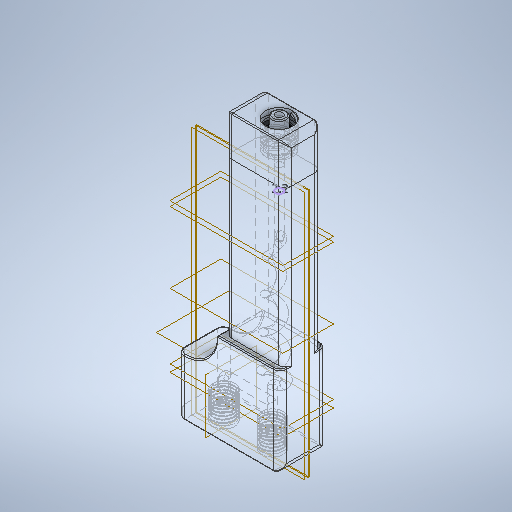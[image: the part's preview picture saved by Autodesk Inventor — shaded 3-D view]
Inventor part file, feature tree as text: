
AUTODESK INVENTOR PART (.ipt)
format: ipt  version: 2025 (Build 290162000, 162)  size: 1,564,672 bytes
history: native  units: mm
features: sketch x27, extrude x15, plane x11, other x9, revolve x6, fillet x3, projected_geometry x1
ambient origin geometry x8: Origin, YZ Plane, XZ Plane, XY Plane, X Axis, Y Axis, Z Axis, Center Point
bodies: Volumenkörper1 (feature_tree), Volumenkörper4 (feature_tree), Volumenkörper5 (feature_tree), Volumenkörper6 (feature_tree), Volumenkörper7 (feature_tree)
feature tree (72):
  extrude  "Extrusion1"  Depth=14.0mm
  extrude  "Extrusion2"  Depth=6.584mm
  plane  "Arbeitsebene4"
  extrude  "Extrusion3"  Depth=2.2mm
  extrude  "Extrusion8"  TaperAngle=0.0deg  [1 undecoded]
  revolve  "Umdrehung3"
  plane  "Arbeitsebene12"
  extrude  "Extrusion10"  Depth=5.0mm TaperAngle=0.0deg
  plane  "Arbeitsebene7"
  extrude  "Extrusion13"  Depth=2.2mm TaperAngle=0.0deg
  extrude  "Extrusion14"  Depth=2.8mm TaperAngle=0.0deg
  other  "Spirale2"
  revolve  "Umdrehung9"
  extrude  "Extrusion15"  Depth=11.0mm
  revolve  "Umdrehung10"
  extrude  "Extrusion16"  Depth=50.0mm TaperAngle=0.0deg
  sketch  "Skizze32"  dims[d91=5.818mm d92=8.0mm d93=-0.061087mm]
  plane  "Arbeitsebene14"
  revolve  "Umdrehung11"
  plane  "Arbeitsebene15"
  plane  "Arbeitsebene16"
  revolve  "Umdrehung12"
  plane  "Arbeitsebene17"
  extrude  "Extrusion19"  TaperAngle=90.0deg  [1 undecoded]
  extrude  "Extrusion20"  Depth=8.15mm
  revolve  "Umdrehung14"
  plane  "Arbeitsebene18"
  other  "Spirale3"
  fillet  "Rundung1"  Radius=13.6mm
  fillet  "Rundung2"  [1 undecoded]
  sketch  "Skizze44"  dims[d111=9.0mm d112=-0.300197mm]
  plane  "Arbeitsebene19"
  other  "Trennen1"
  other  "Körper verschieben1"
  extrude  "Extrusion21"  Depth=7.52mm
  other  "Kombinieren1"
  plane  "Arbeitsebene20"
  extrude  "Extrusion22"  Depth=8.0mm
  extrude  "Extrusion23"  Depth=1.1mm
  fillet  "Rundung4"  Radius=2.2mm
  plane  "Arbeitsebene21"
  other  "Spirale4"
  other  "Spirale5"
  sketch  "Skizze49"  dims[d125=5.0mm d126=10.0mm d127=12.5mm d128=0.061087mm d129=90.0deg d130=90.0deg d131=0.0mm d132=0.0mm]
  other  "Trennen3"
  other  "Körper verschieben2"
  extrude  "Extrusion24"  Depth=54.45mm
  sketch  "Skizze1"  dims[d0=31.0mm d1=14.0mm]
  sketch  "Skizze2"  dims[d2=11.0mm d3=0.0mm d4=6.584mm]
  sketch  "Skizze3"  dims[d6=8.0mm d7=0.0mm d8=2.2mm]
  sketch  "Skizze10"  dims[d9=2.2mm d11=0.0mm]
  sketch  "Skizze11"  dims[d12=8.0mm d13=0.0mm d24=5.0mm d25=0.0mm]
  sketch  "Skizze15"  dims[d26=90.0deg d33=2.2mm d34=0.0mm]
  sketch  "Skizze23"  dims[d35=13.2mm d60=2.8mm d61=0.0mm]
  sketch  "Skizze24"  dims[d62=18.0mm d63=11.0mm]
  sketch  "Skizze25"  dims[d64=1.5mm d65=50.0mm d66=0.0mm]
  sketch  "Skizze27"  dims[d70=8.75mm]
  sketch  "Skizze29"  dims[d71=10.0mm d72=10.0mm d73=35.0mm d74=-0.436332mm d75=90.0deg d76=90.0deg d77=0.0mm d78=0.0mm d80=90.0deg]
  sketch  "Skizze30"  dims[d81=5.9mm d84=8.15mm d86=13.6mm d87=0.0mm d88=90.0deg]
  sketch  "Skizze31"  dims[d89=8.13mm d90=7.52mm]
  sketch  "Skizze35"  dims[d100=0.0mm d102=1.1mm d103=2.2mm]
  sketch  "Skizze36"  dims[d105=90.0deg d106=54.45mm]
  sketch  "Skizze39"  dims[d107=8.37758mm]
  sketch  "Skizze40"  dims[d108=1.55mm]
  projected_geometry  "Projizierte Kontur2"
  sketch  "Skizze43"  dims[d110=4.75mm]
  sketch  "Skizze45"  dims[d113=2.2mm]
  sketch  "Skizze46"  dims[d114=12.5mm d115=0.0mm]
  sketch  "Skizze47"  dims[d116=8.552113mm]
  sketch  "Skizze48"  dims[d117=0.318mm]
  sketch  "Skizze50"  dims[d133=0.3mm]
  sketch  "Skizze51"  dims[d134=2.0mm d136=0.0mm d137=0.0mm d138=0.0mm d139=10.0mm d140=10.0mm d141=0.0mm d142=11.0mm d143=0.0mm d144=20.0mm d145=14.0mm d146=0.0mm d147=0.3mm d148=-1.1mm d156=0.897mm d157=10.0mm d158=73.0mm d159=0.0mm d160=90.0deg d161=90.0deg d162=0.0mm d163=0.0mm d170=0.897mm d171=10.0mm d172=73.0mm d173=0.0mm d174=90.0deg d175=90.0deg d176=0.0mm d177=0.0mm d179=0.0mm d180=0.0mm d181=10.0mm d182=10.0mm d183=0.0mm d22=0.5mm d23=0.872665mm d82=0.872665mm d83=0.5mm d95=0.5mm d96=0.872665mm d97=0.5mm d98=0.872665mm]
note: 3 required parameter values undecoded (feature->parameter linkage not recoverable at this tier; creation-order binding heuristic only, values carry confidence <= 0.55)
